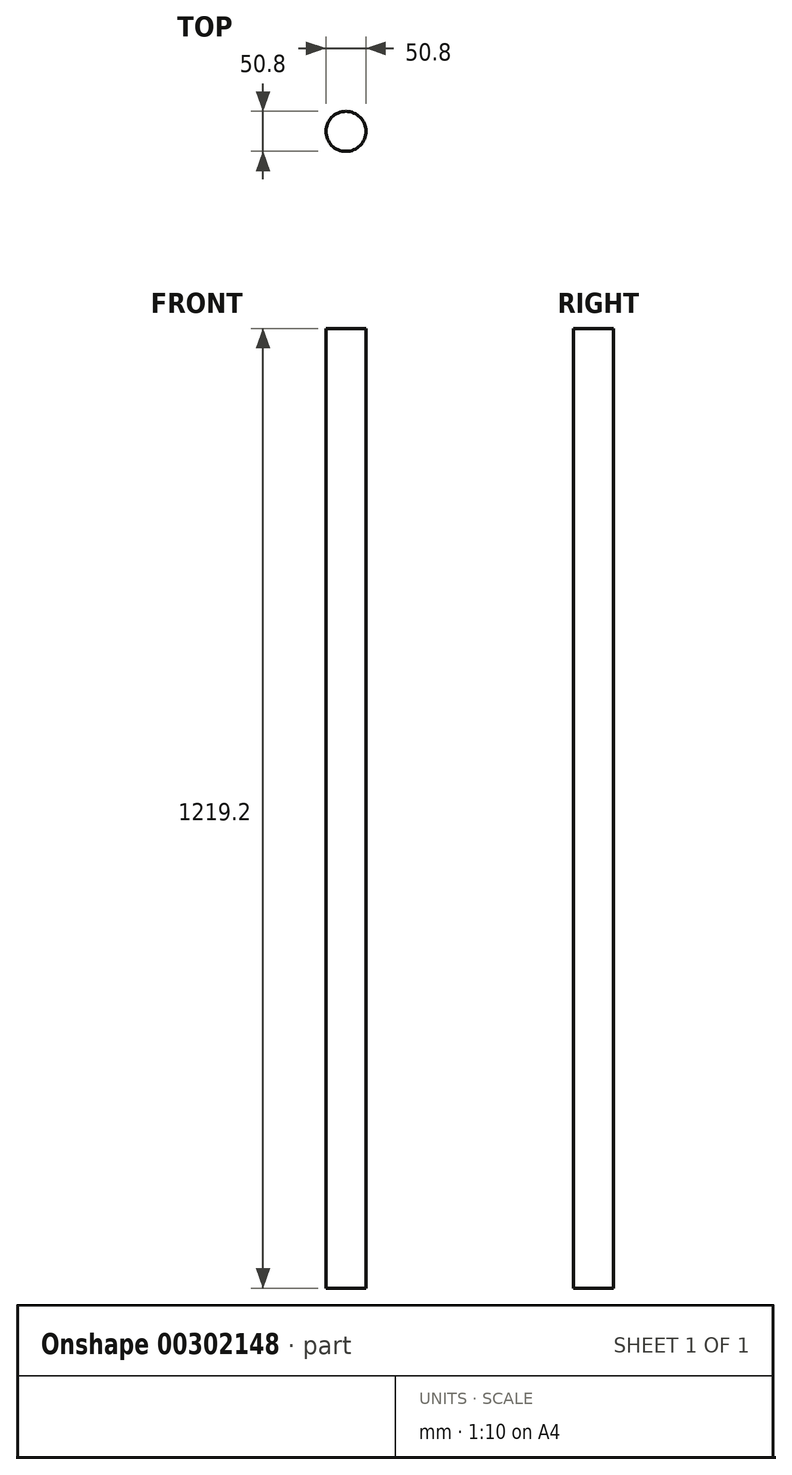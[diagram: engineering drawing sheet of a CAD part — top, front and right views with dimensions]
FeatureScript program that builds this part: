
annotation { "Feature Type Name" : "Feature", "Feature Type Description" : "" }
export const myFeature = defineFeature(function(context is Context, id is Id, definition is map)
    precondition{}
    {
        {
            var Q0;
            Q0=qCreatedBy(makeId("Front.planeOp"),FACE);
            var sketch = newSketch(context, id + "F0", { "sketchPlane" : qUnion([Q0])});
            skLineSegment(sketch, "E0", {"start": v(25.4, 988.79) * mm, "end": v(25.4, -230.41) * mm});
            skLineSegment(sketch, "E1", {"start": v(25.4, -230.41) * mm, "end": v(0, -230.41) * mm});
            skLineSegment(sketch, "E2", {"start": v(25.4, 988.79) * mm, "end": v(0, 988.79) * mm});
            skLineSegment(sketch, "E3", {"start": v(0, 988.79) * mm, "end": v(0, -230.41) * mm});
            skSolve(sketch);
        }
        {
            var Q0;
            Q0 = qSketchRegion(id + "F0", true);
            var Q1;
            Q1=sQuery(id+"F0.wireOp",EDGE,"E3");
            revolve(context, id + "F1", {"entities" : qUnion([Q0]), "axis" : qUnion([Q1]), "revolveType" : RevolveType.FULL});
        }
    });
